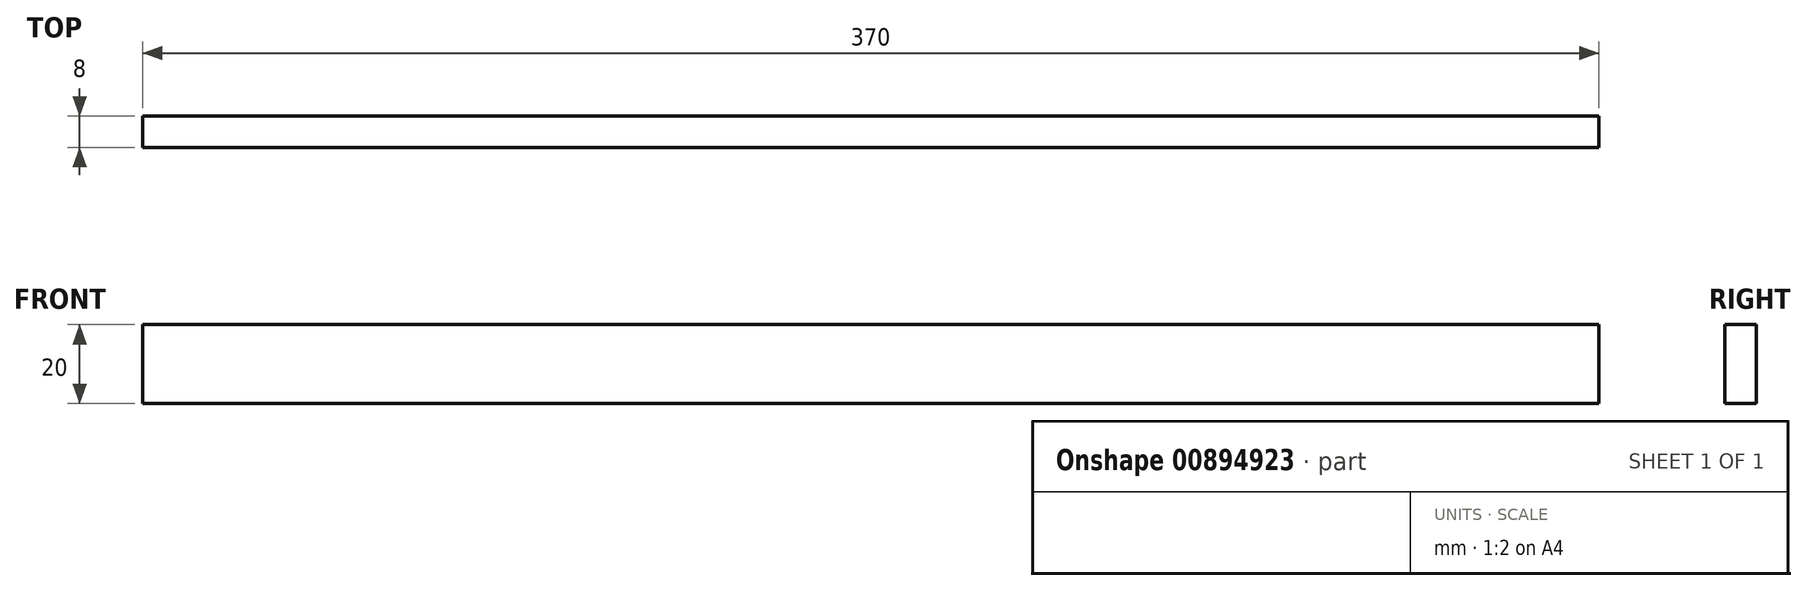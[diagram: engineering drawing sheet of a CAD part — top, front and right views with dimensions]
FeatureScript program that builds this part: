
annotation { "Feature Type Name" : "Feature", "Feature Type Description" : "" }
export const myFeature = defineFeature(function(context is Context, id is Id, definition is map)
    precondition{}
    {
        {
            var Q0;
            Q0=qCreatedBy(makeId("Front.planeOp"),FACE);
            var sketch = newSketch(context, id + "F0", { "sketchPlane" : qUnion([Q0])});
            skLineSegment(sketch, "E0.bottom", {"start": v(-146.14, 20) * mm, "end": v(223.86, 20) * mm});
            skLineSegment(sketch, "E0.top", {"start": v(-146.14, 0) * mm, "end": v(223.86, 0) * mm});
            skLineSegment(sketch, "E0.left", {"start": v(-146.14, 20) * mm, "end": v(-146.14, 0) * mm});
            skLineSegment(sketch, "E0.right", {"start": v(223.86, 20) * mm, "end": v(223.86, 0) * mm});
            skSolve(sketch);
        }
        {
            var Q0;
            Q0=makeQuery(id+"F0.imprint","IMPRINT",FACE,{"disambiguationData":[TD([[makeQuery(id+"F0.imprint","IMPRINT",EDGE,{"derivedFrom":sQuery(id+"F0.wireOp",EDGE,"E0.bottom")}),-1.0]])]});
            extrude(context, id + "F1", {"entities" : qUnion([Q0]), "depth" : 8 * mm, "offsetDistance" : 25 * mm});
        }
    });
